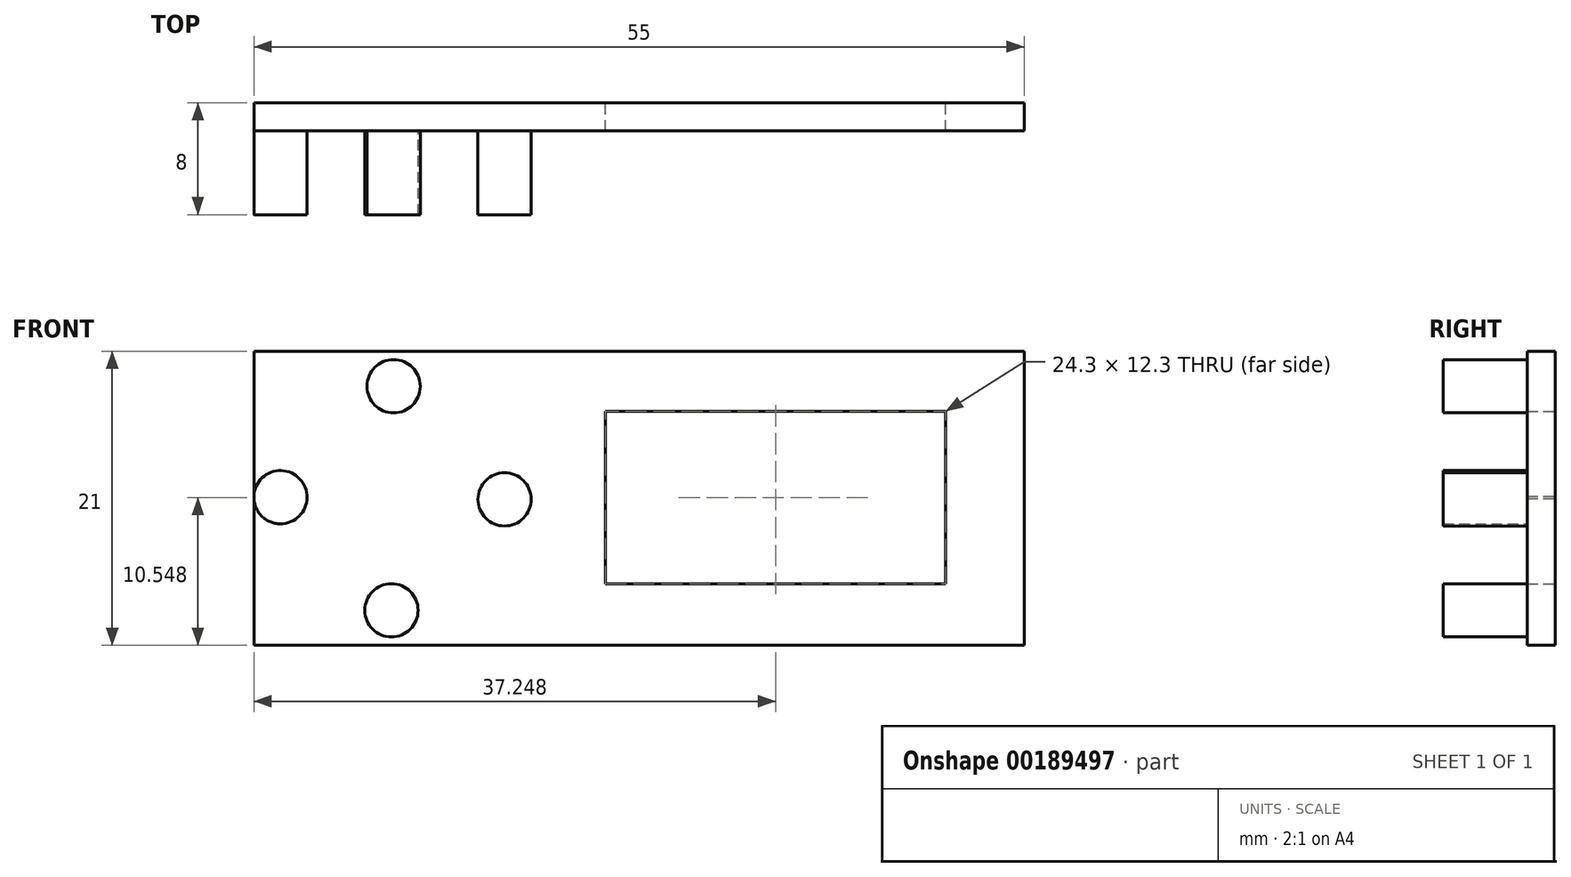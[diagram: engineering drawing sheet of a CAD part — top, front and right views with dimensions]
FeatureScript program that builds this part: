
annotation { "Feature Type Name" : "Feature", "Feature Type Description" : "" }
export const myFeature = defineFeature(function(context is Context, id is Id, definition is map)
    precondition{}
    {
        {
            var Q0;
            Q0=qCreatedBy(makeId("Front.planeOp"),FACE);
            var sketch = newSketch(context, id + "F0", { "sketchPlane" : qUnion([Q0])});
            skLineSegment(sketch, "E0.bottom", {"start": v(-27.58, 6) * mm, "end": v(27.42, 6) * mm});
            skLineSegment(sketch, "E0.top", {"start": v(-27.58, -15) * mm, "end": v(27.42, -15) * mm});
            skLineSegment(sketch, "E0.left", {"start": v(-27.58, 6) * mm, "end": v(-27.58, -15) * mm});
            skLineSegment(sketch, "E0.right", {"start": v(27.42, 6) * mm, "end": v(27.42, -15) * mm});
            skSolve(sketch);
        }
        {
            var Q0;
            Q0 = qSketchRegion(id + "F0", true);
            extrude(context, id + "F1", {"entities" : qUnion([Q0]), "depth" : 2 * mm});
        }
        {
            var Q0;
            Q0=qCreatedBy(makeId("Front.planeOp"),FACE);
            var sketch = newSketch(context, id + "F2", { "sketchPlane" : qUnion([Q0])});
            skCircle(sketch, "E1", {"center": v(-25.68, -4.43) * mm, "radius": 1.9 * mm});
            skCircle(sketch, "E2.1.0", {"center": v(-17.6, 3.5) * mm, "radius": 1.9 * mm});
            skCircle(sketch, "E2.2.0", {"center": v(-9.68, -4.58) * mm, "radius": 1.9 * mm});
            skCircle(sketch, "E2.3.0", {"center": v(-17.76, -12.5) * mm, "radius": 1.9 * mm});
            skPoint(sketch, "E2.center", {"position": v(-17.68, -4.5) * mm});
            skLineSegment(sketch, "E2.anchor1", {"start": v(-17.68, -4.5) * mm, "end": v(-25.68, -4.43) * mm, "construction": true});
            skLineSegment(sketch, "E2.anchor2", {"start": v(-17.68, -4.5) * mm, "end": v(-17.76, -12.5) * mm, "construction": true});
            skSolve(sketch);
        }
        {
            var Q0;
            Q0 = qSketchRegion(id + "F2", true);
            extrude(context, id + "F3", {"entities" : qUnion([Q0]), "operationType" : NewBodyOperationType.ADD, "depth" : 8 * mm});
        }
        {
            var Q0;
            Q0=qCreatedBy(makeId("Front.planeOp"),FACE);
            var sketch = newSketch(context, id + "F4", { "sketchPlane" : qUnion([Q0])});
            skLineSegment(sketch, "E3.bottom", {"start": v(-2.48, 1.7) * mm, "end": v(21.82, 1.7) * mm});
            skLineSegment(sketch, "E3.top", {"start": v(-2.48, -10.6) * mm, "end": v(21.82, -10.6) * mm});
            skLineSegment(sketch, "E3.left", {"start": v(-2.48, 1.7) * mm, "end": v(-2.48, -10.6) * mm});
            skLineSegment(sketch, "E3.right", {"start": v(21.82, 1.7) * mm, "end": v(21.82, -10.6) * mm});
            skSolve(sketch);
        }
        {
            var Q0;
            Q0 = qSketchRegion(id + "F4", true);
            extrude(context, id + "F5", {"entities" : qUnion([Q0]), "operationType" : NewBodyOperationType.REMOVE, "endBound" : BoundingType.THROUGH_ALL, "depth" : 3 * mm});
        }
    });
